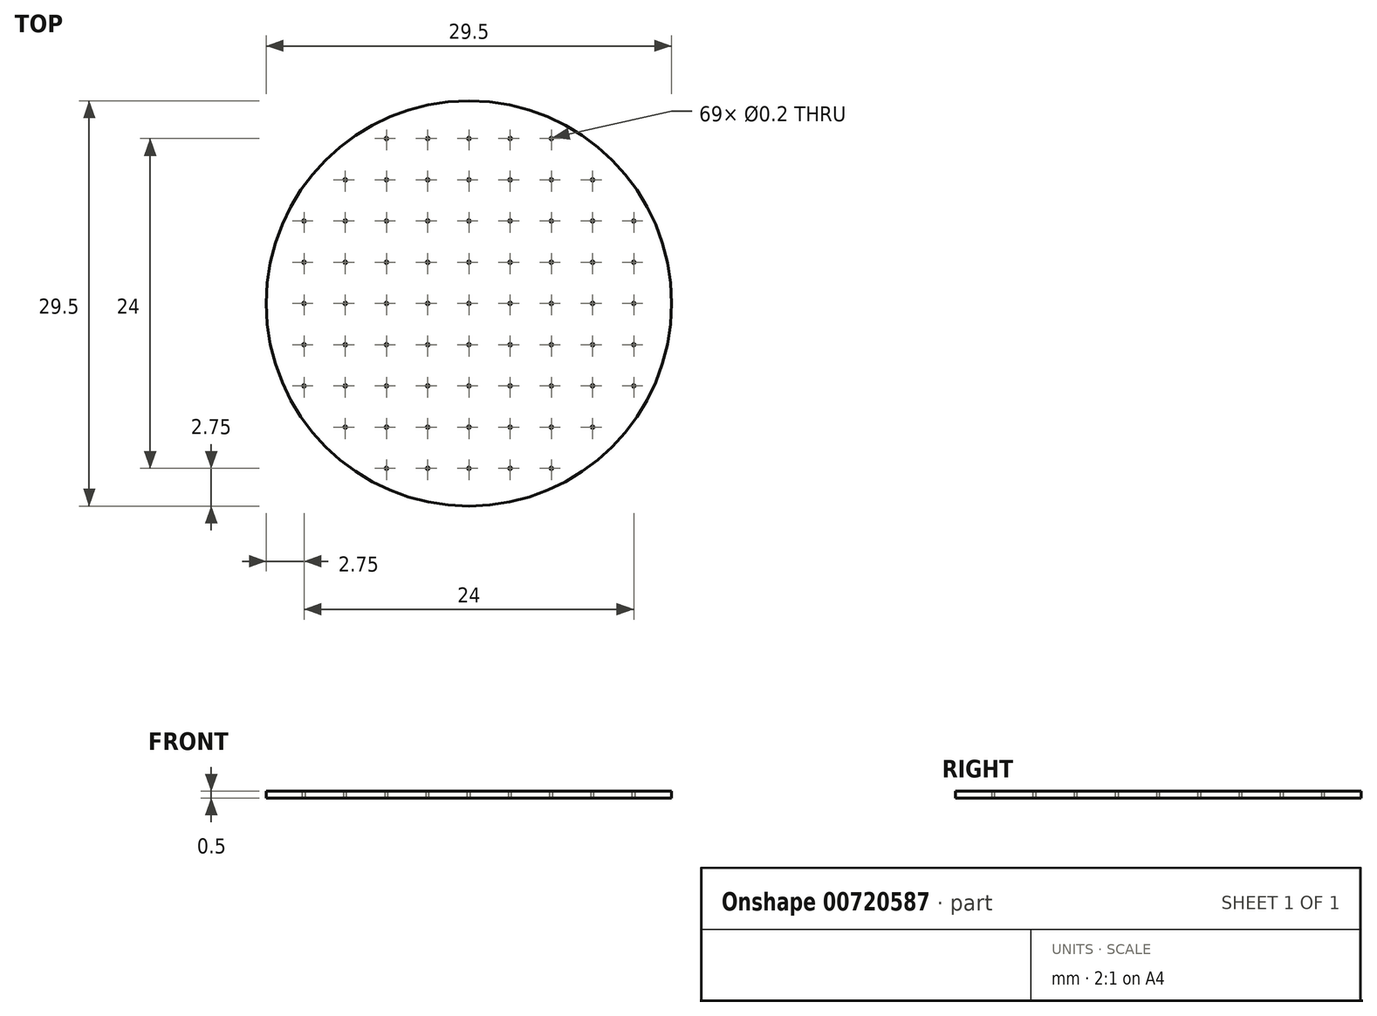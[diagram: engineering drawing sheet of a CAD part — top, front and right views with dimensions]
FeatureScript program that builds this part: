
annotation { "Feature Type Name" : "Feature", "Feature Type Description" : "" }
export const myFeature = defineFeature(function(context is Context, id is Id, definition is map)
    precondition{}
    {
        {
            var Q0;
            Q0=qCreatedBy(makeId("Top.planeOp"),FACE);
            var sketch = newSketch(context, id + "F0", { "sketchPlane" : qUnion([Q0])});
            skCircle(sketch, "E0", {"center": v(0, 0) * mm, "radius": 14.75 * mm});
            skSolve(sketch);
        }
        {
            var Q0;
            Q0 = qSketchRegion(id + "F0", true);
            extrude(context, id + "F1", {"entities" : qUnion([Q0]), "depth" : 0.5 * mm, "offsetDistance" : 25 * mm, "symmetric" : true});
        }
        {
            var Q0;
            Q0=makeQuery(id+"F1.opExtrude","CAP_FACE",FACE,{"disambiguationData":[OSD([sQuery(id+"F0.wireOp",EDGE,"E0")])],"isStart":false});
            var sketch = newSketch(context, id + "F2", { "sketchPlane" : qUnion([Q0])});
            skPoint(sketch, "E1", {"position": v(0, 0) * mm});
            skPoint(sketch, "E2.0.1.0", {"position": v(0, 3) * mm});
            skPoint(sketch, "E2.0.2.0", {"position": v(0, 6) * mm});
            skPoint(sketch, "E2.0.3.0", {"position": v(0, 9) * mm});
            skPoint(sketch, "E2.0.4.0", {"position": v(0, 12) * mm});
            skPoint(sketch, "E2.1.0.0", {"position": v(3, 0) * mm});
            skPoint(sketch, "E2.1.1.0", {"position": v(3, 3) * mm});
            skPoint(sketch, "E2.1.2.0", {"position": v(3, 6) * mm});
            skPoint(sketch, "E2.1.3.0", {"position": v(3, 9) * mm});
            skPoint(sketch, "E2.1.4.0", {"position": v(3, 12) * mm});
            skPoint(sketch, "E2.2.0.0", {"position": v(6, 0) * mm});
            skPoint(sketch, "E2.2.1.0", {"position": v(6, 3) * mm});
            skPoint(sketch, "E2.2.2.0", {"position": v(6, 6) * mm});
            skPoint(sketch, "E2.2.3.0", {"position": v(6, 9) * mm});
            skPoint(sketch, "E2.2.4.0", {"position": v(6, 12) * mm});
            skPoint(sketch, "E2.3.0.0", {"position": v(9, 0) * mm});
            skPoint(sketch, "E2.3.1.0", {"position": v(9, 3) * mm});
            skPoint(sketch, "E2.3.2.0", {"position": v(9, 6) * mm});
            skPoint(sketch, "E2.3.3.0", {"position": v(9, 9) * mm});
            skPoint(sketch, "E2.3.4.0", {"position": v(9, 12) * mm});
            skPoint(sketch, "E2.4.0.0", {"position": v(12, 0) * mm});
            skPoint(sketch, "E2.4.1.0", {"position": v(12, 3) * mm});
            skPoint(sketch, "E2.4.2.0", {"position": v(12, 6) * mm});
            skPoint(sketch, "E2.4.3.0", {"position": v(12, 9) * mm});
            skPoint(sketch, "E2.4.4.0", {"position": v(12, 12) * mm});
            skLineSegment(sketch, "E2.direction1", {"start": v(0, 0) * mm, "end": v(3, 0) * mm, "construction": true});
            skLineSegment(sketch, "E2.direction2", {"start": v(0, 0) * mm, "end": v(0, 3) * mm, "construction": true});
            skPoint(sketch, "E3.1.0", {"position": v(-9, 0) * mm});
            skPoint(sketch, "E3.1.1", {"position": v(-12, 0) * mm});
            skPoint(sketch, "E3.1.3", {"position": v(-12, 12) * mm});
            skPoint(sketch, "E3.1.4", {"position": v(-9, 12) * mm});
            skPoint(sketch, "E3.1.5", {"position": v(-6, 12) * mm});
            skPoint(sketch, "E3.1.6", {"position": v(-3, 12) * mm});
            skPoint(sketch, "E3.1.8", {"position": v(-12, 9) * mm});
            skPoint(sketch, "E3.1.9", {"position": v(-9, 9) * mm});
            skPoint(sketch, "E3.1.10", {"position": v(-6, 9) * mm});
            skPoint(sketch, "E3.1.11", {"position": v(-3, 9) * mm});
            skPoint(sketch, "E3.1.13", {"position": v(-12, 3) * mm});
            skPoint(sketch, "E3.1.14", {"position": v(-12, 6) * mm});
            skPoint(sketch, "E3.1.16", {"position": v(-9, 6) * mm});
            skPoint(sketch, "E3.1.17", {"position": v(-3, 6) * mm});
            skPoint(sketch, "E3.1.18", {"position": v(-6, 6) * mm});
            skPoint(sketch, "E3.1.20", {"position": v(-3, 0) * mm});
            skPoint(sketch, "E3.1.21", {"position": v(-6, 0) * mm});
            skPoint(sketch, "E3.1.22", {"position": v(-3, 3) * mm});
            skPoint(sketch, "E3.1.23", {"position": v(-6, 3) * mm});
            skPoint(sketch, "E3.1.24", {"position": v(-9, 3) * mm});
            skLineSegment(sketch, "E3.1.26", {"start": v(0, 0) * mm, "end": v(-3, 0) * mm, "construction": true});
            skPoint(sketch, "E3.2.0", {"position": v(0, -9) * mm});
            skPoint(sketch, "E3.2.1", {"position": v(0, -12) * mm});
            skPoint(sketch, "E3.2.2", {"position": v(-3, 0) * mm});
            skPoint(sketch, "E3.2.3", {"position": v(-12, -12) * mm});
            skPoint(sketch, "E3.2.4", {"position": v(-12, -9) * mm});
            skPoint(sketch, "E3.2.5", {"position": v(-12, -6) * mm});
            skPoint(sketch, "E3.2.6", {"position": v(-12, -3) * mm});
            skPoint(sketch, "E3.2.7", {"position": v(-12, 0) * mm});
            skPoint(sketch, "E3.2.8", {"position": v(-9, -12) * mm});
            skPoint(sketch, "E3.2.9", {"position": v(-9, -9) * mm});
            skPoint(sketch, "E3.2.10", {"position": v(-9, -6) * mm});
            skPoint(sketch, "E3.2.11", {"position": v(-9, -3) * mm});
            skPoint(sketch, "E3.2.12", {"position": v(-9, 0) * mm});
            skPoint(sketch, "E3.2.13", {"position": v(-3, -12) * mm});
            skPoint(sketch, "E3.2.14", {"position": v(-6, -12) * mm});
            skPoint(sketch, "E3.2.15", {"position": v(-6, 0) * mm});
            skPoint(sketch, "E3.2.16", {"position": v(-6, -9) * mm});
            skPoint(sketch, "E3.2.17", {"position": v(-6, -3) * mm});
            skPoint(sketch, "E3.2.18", {"position": v(-6, -6) * mm});
            skPoint(sketch, "E3.2.20", {"position": v(0, -3) * mm});
            skPoint(sketch, "E3.2.21", {"position": v(0, -6) * mm});
            skPoint(sketch, "E3.2.22", {"position": v(-3, -3) * mm});
            skPoint(sketch, "E3.2.23", {"position": v(-3, -6) * mm});
            skPoint(sketch, "E3.2.24", {"position": v(-3, -9) * mm});
            skLineSegment(sketch, "E3.2.25", {"start": v(0, 0) * mm, "end": v(-3, 0) * mm, "construction": true});
            skLineSegment(sketch, "E3.2.26", {"start": v(0, 0) * mm, "end": v(0, -3) * mm, "construction": true});
            skPoint(sketch, "E3.3.2", {"position": v(0, -3) * mm});
            skPoint(sketch, "E3.3.3", {"position": v(12, -12) * mm});
            skPoint(sketch, "E3.3.4", {"position": v(9, -12) * mm});
            skPoint(sketch, "E3.3.5", {"position": v(6, -12) * mm});
            skPoint(sketch, "E3.3.6", {"position": v(3, -12) * mm});
            skPoint(sketch, "E3.3.7", {"position": v(0, -12) * mm});
            skPoint(sketch, "E3.3.8", {"position": v(12, -9) * mm});
            skPoint(sketch, "E3.3.9", {"position": v(9, -9) * mm});
            skPoint(sketch, "E3.3.10", {"position": v(6, -9) * mm});
            skPoint(sketch, "E3.3.11", {"position": v(3, -9) * mm});
            skPoint(sketch, "E3.3.12", {"position": v(0, -9) * mm});
            skPoint(sketch, "E3.3.13", {"position": v(12, -3) * mm});
            skPoint(sketch, "E3.3.14", {"position": v(12, -6) * mm});
            skPoint(sketch, "E3.3.15", {"position": v(0, -6) * mm});
            skPoint(sketch, "E3.3.16", {"position": v(9, -6) * mm});
            skPoint(sketch, "E3.3.17", {"position": v(3, -6) * mm});
            skPoint(sketch, "E3.3.18", {"position": v(6, -6) * mm});
            skPoint(sketch, "E3.3.22", {"position": v(3, -3) * mm});
            skPoint(sketch, "E3.3.23", {"position": v(6, -3) * mm});
            skPoint(sketch, "E3.3.24", {"position": v(9, -3) * mm});
            skLineSegment(sketch, "E3.3.25", {"start": v(0, 0) * mm, "end": v(0, -3) * mm, "construction": true});
            skSolve(sketch);
        }
        {
            var Q0;
            Q0=sQuery(id+"F2.wireOp",VERTEX,"E3.3.3");
            var Q1;
            Q1=sQuery(id+"F2.wireOp",VERTEX,"E3.3.10");
            var Q2;
            Q2=sQuery(id+"F2.wireOp",VERTEX,"E2.2.0.0");
            var Q3;
            Q3=sQuery(id+"F2.wireOp",VERTEX,"E2.3.1.0");
            var Q4;
            Q4=sQuery(id+"F2.wireOp",VERTEX,"E2.0.4.0");
            var Q5;
            Q5=sQuery(id+"F2.wireOp",VERTEX,"E3.1.23");
            var Q6;
            Q6=sQuery(id+"F2.wireOp",VERTEX,"E3.2.14");
            var Q7;
            Q7=sQuery(id+"F2.wireOp",VERTEX,"E3.2.5");
            var Q8;
            Q8=sQuery(id+"F2.wireOp",VERTEX,"E2.2.4.0");
            var Q9;
            Q9=sQuery(id+"F2.wireOp",VERTEX,"E3.2.3");
            var Q10;
            Q10=sQuery(id+"F2.wireOp",VERTEX,"E2.4.1.0");
            var Q11;
            Q11=sQuery(id+"F2.wireOp",VERTEX,"E3.1.5");
            var Q12;
            Q12=sQuery(id+"F2.wireOp",VERTEX,"E2.1.2.0");
            var Q13;
            Q13=sQuery(id+"F2.wireOp",VERTEX,"E2.0.3.0");
            var Q14;
            Q14=sQuery(id+"F2.wireOp",VERTEX,"E2.4.3.0");
            var Q15;
            Q15=sQuery(id+"F2.wireOp",VERTEX,"E3.1.14");
            var Q16;
            Q16=sQuery(id+"F2.wireOp",VERTEX,"E3.2.9");
            var Q17;
            Q17=sQuery(id+"F2.wireOp",VERTEX,"E2.3.0.0");
            var Q18;
            Q18=sQuery(id+"F2.wireOp",VERTEX,"E3.3.16");
            var Q19;
            Q19=sQuery(id+"F2.wireOp",VERTEX,"E2.2.1.0");
            var Q20;
            Q20=sQuery(id+"F2.wireOp",VERTEX,"E2.0.1.0");
            var Q21;
            Q21=sQuery(id+"F2.wireOp",VERTEX,"E3.1.18");
            var Q22;
            Q22=sQuery(id+"F2.wireOp",VERTEX,"E3.3.5");
            var Q23;
            Q23=sQuery(id+"F2.wireOp",VERTEX,"E3.2.15");
            var Q24;
            Q24=sQuery(id+"F2.wireOp",VERTEX,"E3.1.24");
            var Q25;
            Q25=sQuery(id+"F2.wireOp",VERTEX,"E3.1.8");
            var Q26;
            Q26=sQuery(id+"F2.wireOp",VERTEX,"E2.3.2.0");
            var Q27;
            Q27=sQuery(id+"F2.wireOp",VERTEX,"E3.3.22");
            var Q28;
            Q28=sQuery(id+"F2.wireOp",VERTEX,"E3.3.6");
            var Q29;
            Q29=sQuery(id+"F2.wireOp",VERTEX,"E3.1.3");
            var Q30;
            Q30=sQuery(id+"F2.wireOp",VERTEX,"E2.2.2.0");
            var Q31;
            Q31=sQuery(id+"F2.wireOp",VERTEX,"E3.3.17");
            var Q32;
            Q32=sQuery(id+"F2.wireOp",VERTEX,"E2.4.0.0");
            var Q33;
            Q33=sQuery(id+"F2.wireOp",VERTEX,"E3.2.10");
            var Q34;
            Q34=sQuery(id+"F2.wireOp",VERTEX,"E2.0.2.0");
            var Q35;
            Q35=sQuery(id+"F2.wireOp",VERTEX,"E2.4.4.0");
            var Q36;
            Q36=sQuery(id+"F2.wireOp",VERTEX,"E2.1.3.0");
            var Q37;
            Q37=sQuery(id+"F2.wireOp",VERTEX,"E3.3.13");
            var Q38;
            Q38=sQuery(id+"F2.wireOp",VERTEX,"E3.2.22");
            var Q39;
            Q39=sQuery(id+"F2.wireOp",VERTEX,"E3.2.6");
            var Q40;
            Q40=sQuery(id+"F2.wireOp",VERTEX,"E2.1.1.0");
            var Q41;
            Q41=sQuery(id+"F2.wireOp",VERTEX,"E3.2.13");
            var Q42;
            Q42=sQuery(id+"F2.wireOp",VERTEX,"E3.2.4");
            var Q43;
            Q43=sQuery(id+"F2.wireOp",VERTEX,"E3.1.22");
            var Q44;
            Q44=sQuery(id+"F2.wireOp",VERTEX,"E3.1.13");
            var Q45;
            Q45=sQuery(id+"F2.wireOp",VERTEX,"E3.1.6");
            var Q46;
            Q46=sQuery(id+"F2.wireOp",VERTEX,"E2.4.2.0");
            var Q47;
            Q47=sQuery(id+"F2.wireOp",VERTEX,"E2.1.0.0");
            var Q48;
            Q48=sQuery(id+"F2.wireOp",VERTEX,"E3.3.11");
            var Q49;
            Q49=sQuery(id+"F2.wireOp",VERTEX,"E3.3.4");
            var Q50;
            Q50=sQuery(id+"F2.wireOp",VERTEX,"E3.2.16");
            var Q51;
            Q51=sQuery(id+"F2.wireOp",VERTEX,"E3.2.0");
            var Q52;
            Q52=sQuery(id+"F2.wireOp",VERTEX,"E3.1.9");
            var Q53;
            Q53=sQuery(id+"F2.wireOp",VERTEX,"E2.3.3.0");
            var Q54;
            Q54=sQuery(id+"F2.wireOp",VERTEX,"E3.3.23");
            var Q55;
            Q55=sQuery(id+"F2.wireOp",VERTEX,"E3.2.25.end");
            var Q56;
            Q56=sQuery(id+"F2.wireOp",VERTEX,"E3.2.26.end");
            var Q57;
            Q57=sQuery(id+"F2.wireOp",VERTEX,"E3.3.25.start");
            var Q58;
            Q58=sQuery(id+"F2.wireOp",VERTEX,"E3.1.16");
            var Q59;
            Q59=sQuery(id+"F2.wireOp",VERTEX,"E3.1.0");
            var Q60;
            Q60=sQuery(id+"F2.wireOp",VERTEX,"E2.1.4.0");
            var Q61;
            Q61=sQuery(id+"F2.wireOp",VERTEX,"E3.3.14");
            var Q62;
            Q62=sQuery(id+"F2.wireOp",VERTEX,"E3.2.23");
            var Q63;
            Q63=sQuery(id+"F2.wireOp",VERTEX,"E3.2.17");
            var Q64;
            Q64=sQuery(id+"F2.wireOp",VERTEX,"E3.2.1");
            var Q65;
            Q65=sQuery(id+"F2.wireOp",VERTEX,"E3.1.10");
            var Q66;
            Q66=sQuery(id+"F2.wireOp",VERTEX,"E2.3.4.0");
            var Q67;
            Q67=sQuery(id+"F2.wireOp",VERTEX,"E3.3.24");
            var Q68;
            Q68=sQuery(id+"F2.wireOp",VERTEX,"E3.3.8");
            var Q69;
            Q69=sQuery(id+"F2.wireOp",VERTEX,"E3.1.17");
            var Q70;
            Q70=sQuery(id+"F2.wireOp",VERTEX,"E3.1.1");
            var Q71;
            Q71=sQuery(id+"F2.wireOp",VERTEX,"E3.3.15");
            var Q72;
            Q72=sQuery(id+"F2.wireOp",VERTEX,"E3.2.24");
            var Q73;
            Q73=sQuery(id+"F2.wireOp",VERTEX,"E3.2.8");
            var Q74;
            Q74=sQuery(id+"F2.wireOp",VERTEX,"E3.2.18");
            var Q75;
            Q75=sQuery(id+"F2.wireOp",VERTEX,"E3.2.11");
            var Q76;
            Q76=sQuery(id+"F2.wireOp",VERTEX,"E3.1.11");
            var Q77;
            Q77=sQuery(id+"F2.wireOp",VERTEX,"E3.1.4");
            var Q78;
            Q78=sQuery(id+"F2.wireOp",VERTEX,"E2.2.3.0");
            var Q79;
            Q79=sQuery(id+"F2.wireOp",VERTEX,"E3.3.18");
            var Q80;
            Q80=sQuery(id+"F2.wireOp",VERTEX,"E3.3.9");
            var Q81;
            Q81=makeQuery(id+"F1.opExtrude","SWEPT_BODY",BODY,{"disambiguationData":[OSD([sQuery(id+"F0.wireOp",EDGE,"E0")])]});
            hole(context, id + "F3", {"style" : HoleStyle.SIMPLE, "endStyle" : HoleEndStyle.BLIND, "holeDiameter" : 0.2 * mm, "majorDiameter" : 3 * mm, "holeDepth" : 5 * mm, "isTappedThrough" : true, "tappedDepth" : 3.5 * mm, "tapClearance" : 3, "locations" : qUnion([Q0, Q1, Q2, Q3, Q4, Q5, Q6, Q7, Q8, Q9, Q10, Q11, Q12, Q13, Q14, Q15, Q16, Q17, Q18, Q19, Q20, Q21, Q22, Q23, Q24, Q25, Q26, Q27, Q28, Q29, Q30, Q31, Q32, Q33, Q34, Q35, Q36, Q37, Q38, Q39, Q40, Q41, Q42, Q43, Q44, Q45, Q46, Q47, Q48, Q49, Q50, Q51, Q52, Q53, Q54, Q55, Q56, Q57, Q58, Q59, Q60, Q61, Q62, Q63, Q64, Q65, Q66, Q67, Q68, Q69, Q70, Q71, Q72, Q73, Q74, Q75, Q76, Q77, Q78, Q79, Q80]), "scope" : qUnion([Q81])});
        }
    });
